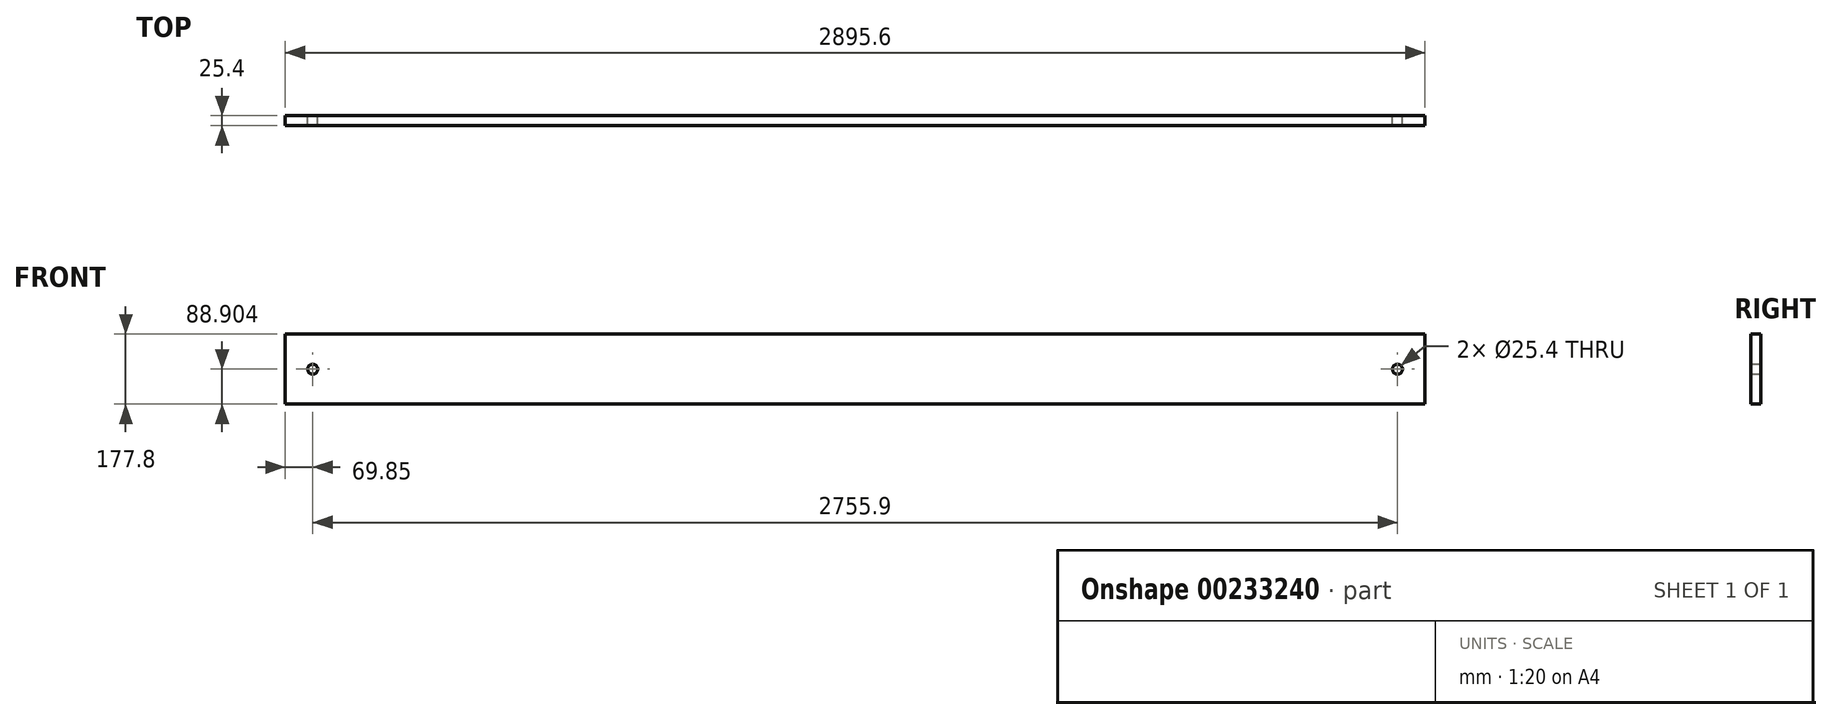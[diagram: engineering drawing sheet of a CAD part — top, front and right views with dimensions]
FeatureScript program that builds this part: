
annotation { "Feature Type Name" : "Feature", "Feature Type Description" : "" }
export const myFeature = defineFeature(function(context is Context, id is Id, definition is map)
    precondition{}
    {
        {
            var Q0;
            Q0=qCreatedBy(makeId("Front.planeOp"),FACE);
            var sketch = newSketch(context, id + "F0", { "sketchPlane" : qUnion([Q0])});
            skLineSegment(sketch, "E0.bottom", {"start": v(-1378.19, -180.37) * mm, "end": v(1517.41, -180.37) * mm});
            skLineSegment(sketch, "E0.top", {"start": v(-1378.19, -2.57) * mm, "end": v(1517.41, -2.57) * mm});
            skLineSegment(sketch, "E0.left", {"start": v(-1378.19, -180.37) * mm, "end": v(-1378.19, -2.57) * mm});
            skLineSegment(sketch, "E0.right", {"start": v(1517.41, -180.37) * mm, "end": v(1517.41, -2.57) * mm});
            skCircle(sketch, "E1", {"center": v(-1308.34, -91.47) * mm, "radius": 12.7 * mm});
            skCircle(sketch, "E2", {"center": v(1447.56, -91.47) * mm, "radius": 12.7 * mm});
            skSolve(sketch);
        }
        {
            var Q0;
            Q0 = qSketchRegion(id + "F0", true);
            extrude(context, id + "F1", {"entities" : qUnion([Q0]), "depth" : 25.4 * mm});
        }
    });
